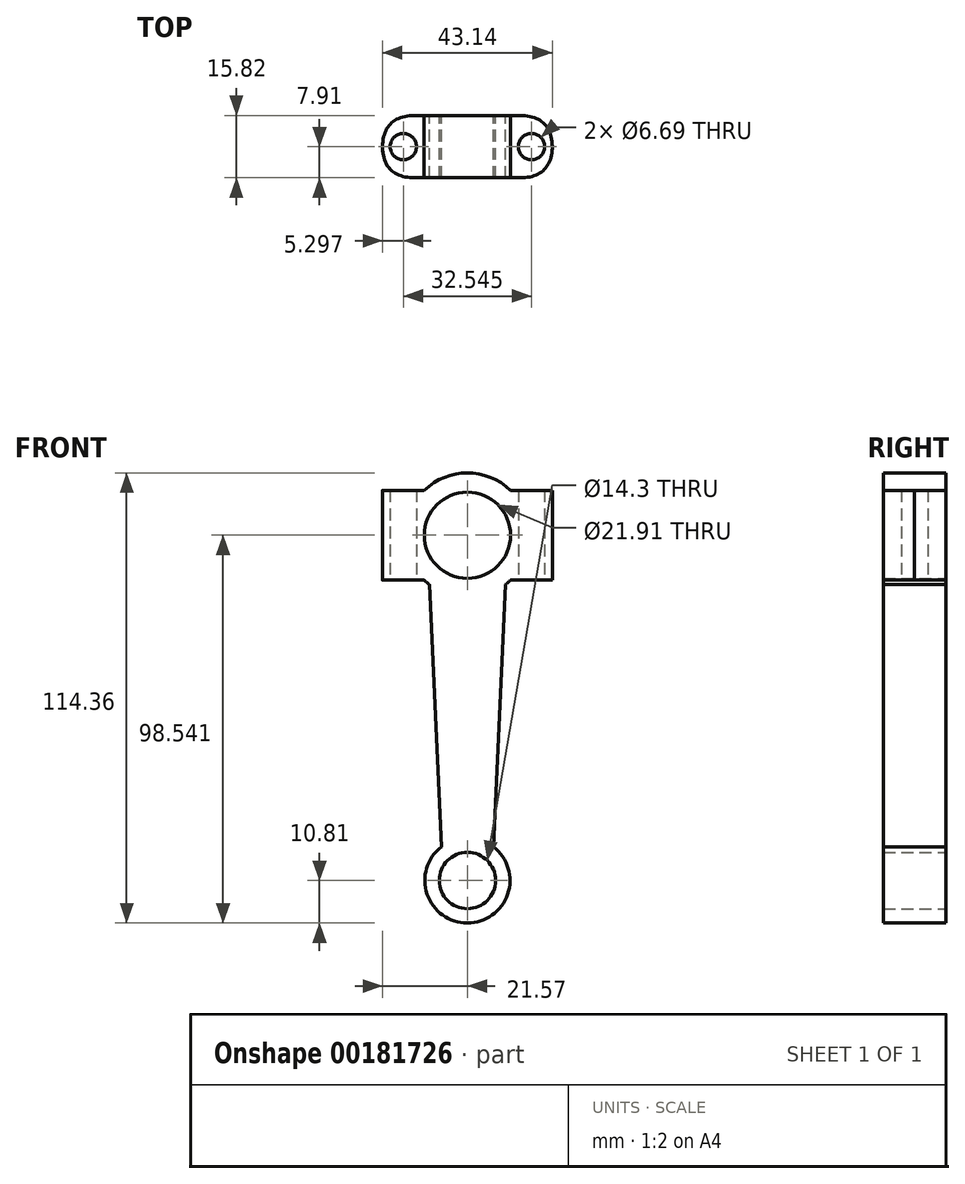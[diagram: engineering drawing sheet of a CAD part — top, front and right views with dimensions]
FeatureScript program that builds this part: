
annotation { "Feature Type Name" : "Feature", "Feature Type Description" : "" }
export const myFeature = defineFeature(function(context is Context, id is Id, definition is map)
    precondition{}
    {
        {
            var Q0;
            Q0=qCreatedBy(makeId("Front.planeOp"),FACE);
            var sketch = newSketch(context, id + "F0", { "sketchPlane" : qUnion([Q0])});
            skCircle(sketch, "E0", {"center": v(0, 0) * mm, "radius": 7.15 * mm});
            skCircle(sketch, "E1", {"center": v(0, 87.73) * mm, "radius": 10.95 * mm});
            skLineSegment(sketch, "E2", {"start": v(-9.61, 75.17) * mm, "end": v(-6.6, 8.56) * mm});
            skLineSegment(sketch, "E3", {"start": v(9.61, 75.17) * mm, "end": v(6.6, 8.56) * mm});
            skArc(sketch, "E4", {"start": v(-6.6, 8.56) * mm, "mid": v(0, -10.81) * mm, "end": v(6.6, 8.56) * mm});
            skArc(sketch, "E5", {"start": v(-10.97, 76.34) * mm, "mid": v(-10.31, 75.74) * mm, "end": v(-9.61, 75.17) * mm});
            skArc(sketch, "E6", {"start": v(9.61, 75.17) * mm, "mid": v(10.31, 75.74) * mm, "end": v(10.97, 76.34) * mm});
            skArc(sketch, "E7", {"start": v(10.97, 99.12) * mm, "mid": v(0, 103.55) * mm, "end": v(-10.97, 99.12) * mm});
            skLineSegment(sketch, "E8", {"start": v(-9.61, 75.17) * mm, "end": v(9.61, 75.17) * mm, "construction": true});
            skLineSegment(sketch, "E9", {"start": v(-10.97, 99.12) * mm, "end": v(-10.97, 76.34) * mm, "construction": true});
            skLineSegment(sketch, "E10", {"start": v(10.97, 99.12) * mm, "end": v(10.97, 76.34) * mm, "construction": true});
            skLineSegment(sketch, "E11", {"start": v(-10.97, 99.12) * mm, "end": v(-21.57, 99.12) * mm});
            skLineSegment(sketch, "E12", {"start": v(-10.97, 76.34) * mm, "end": v(-21.57, 76.34) * mm});
            skLineSegment(sketch, "E13", {"start": v(-21.57, 76.34) * mm, "end": v(-21.57, 99.12) * mm});
            skLineSegment(sketch, "E14", {"start": v(10.97, 76.34) * mm, "end": v(21.57, 76.34) * mm});
            skLineSegment(sketch, "E15", {"start": v(10.97, 99.12) * mm, "end": v(21.57, 99.12) * mm});
            skLineSegment(sketch, "E16", {"start": v(21.57, 99.12) * mm, "end": v(21.57, 76.34) * mm});
            skLineSegment(sketch, "E17", {"start": v(-6.6, 8.56) * mm, "end": v(6.6, 8.56) * mm, "construction": true});
            skSolve(sketch);
        }
        {
            var Q0;
            Q0=makeQuery(id+"F0.imprint","IMPRINT",FACE,{"disambiguationData":[TD([[makeQuery(id+"F0.imprint","IMPRINT",EDGE,{"derivedFrom":sQuery(id+"F0.wireOp",EDGE,"E0")}),-1.0]])]});
            extrude(context, id + "F1", {"entities" : qUnion([Q0]), "endBound" : BoundingType.SYMMETRIC, "depth" : 15.82 * mm});
        }
        {
            var Q0;
            Q0=makeQuery(id+"F1.opExtrude","CAP_EDGE",EDGE,{"disambiguationData":[OSD([sQuery(id+"F0.wireOp",EDGE,"deAWyZeW-K4qn-GDww-XcYt-bZkXSAc4fZ0b")])],"isStart":false});
            var Q1;
            Q1=makeQuery(id+"F1.opExtrude","CAP_EDGE",EDGE,{"disambiguationData":[OSD([sQuery(id+"F0.wireOp",EDGE,"deAWyZeW-K4qn-GDww-XcYt-bZkXSAc4fZ0b")])],"isStart":true});
            var Q2;
            Q2=makeQuery(id+"F1.opExtrude","CAP_EDGE",EDGE,{"disambiguationData":[OSD([sQuery(id+"F0.wireOp",EDGE,"D5Skwm7B-S90H-LKf2-ryvi-PfwuobEKBy49")])],"isStart":true});
            var Q3;
            Q3=makeQuery(id+"F1.opExtrude","CAP_EDGE",EDGE,{"disambiguationData":[OSD([sQuery(id+"F0.wireOp",EDGE,"D5Skwm7B-S90H-LKf2-ryvi-PfwuobEKBy49")])],"isStart":false});
            var Q4;
            Q4=makeQuery(id+"F1.opExtrude","CAP_EDGE",EDGE,{"disambiguationData":[OSD([sQuery(id+"F0.wireOp",EDGE,"E13")])],"isStart":false});
            var Q5;
            Q5=makeQuery(id+"F1.opExtrude","CAP_EDGE",EDGE,{"disambiguationData":[OSD([sQuery(id+"F0.wireOp",EDGE,"E13")])],"isStart":true});
            var Q6;
            Q6=makeQuery(id+"F1.opExtrude","CAP_EDGE",EDGE,{"disambiguationData":[OSD([sQuery(id+"F0.wireOp",EDGE,"E16")])],"isStart":false});
            var Q7;
            Q7=makeQuery(id+"F1.opExtrude","CAP_EDGE",EDGE,{"disambiguationData":[OSD([sQuery(id+"F0.wireOp",EDGE,"E16")])],"isStart":true});
            fillet(context, id + "F2", {"entities" : qUnion([Q0, Q1, Q2, Q3, Q4, Q5, Q6, Q7]), "radius" : 8.25 * mm, "tangentPropagation" : true, "rho" : 0.5, "crossSection" : FilletCrossSection.CONIC, "allowEdgeOverflow" : false});
        }
        {
            var Q0;
            Q0=qCreatedBy(makeId("Top.planeOp"),FACE);
            var sketch = newSketch(context, id + "F3", { "sketchPlane" : qUnion([Q0])});
            skLineSegment(sketch, "E18", {"start": v(-21.57, 0) * mm, "end": v(-10.98, 0) * mm, "construction": true});
            skLineSegment(sketch, "E19", {"start": v(21.57, 0) * mm, "end": v(10.98, 0) * mm, "construction": true});
            skCircle(sketch, "E20", {"center": v(-16.27, 0) * mm, "radius": 3.34 * mm});
            skCircle(sketch, "E21", {"center": v(16.27, 0) * mm, "radius": 3.34 * mm});
            skSolve(sketch);
        }
        {
            var Q0;
            Q0 = qSketchRegion(id + "F3", true);
            extrude(context, id + "F4", {"entities" : qUnion([Q0]), "operationType" : NewBodyOperationType.REMOVE, "endBound" : BoundingType.THROUGH_ALL, "depth" : 25.4 * mm});
        }
    });
